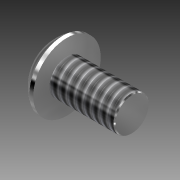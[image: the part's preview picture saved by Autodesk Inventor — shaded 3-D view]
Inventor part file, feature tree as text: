
AUTODESK INVENTOR PART (.ipt)
format: ipt  version: 2012 (Build 160160000, 160)  size: 119,808 bytes
history: native  units: in
note: dims shown in document units (in); Inventor stores cm internally (conversion verified against a paired STEP export)
features: other x1, imported_body x1, thread x1
ambient origin geometry x8: Origin, YZ Plane, XZ Plane, XY Plane, X Axis, Y Axis, Z Axis, Center Point
feature tree (3):
  parser-record x1  (decoder bookkeeping rows leaked as tree rows — omitted from the tree; the rows remain in map.json)
  imported_body  "Base1"
  thread  "Thread1"  [1 undecoded]
note: 1 required parameter value undecoded (feature->parameter linkage not recoverable at this tier; creation-order binding heuristic only, values carry confidence <= 0.55)
